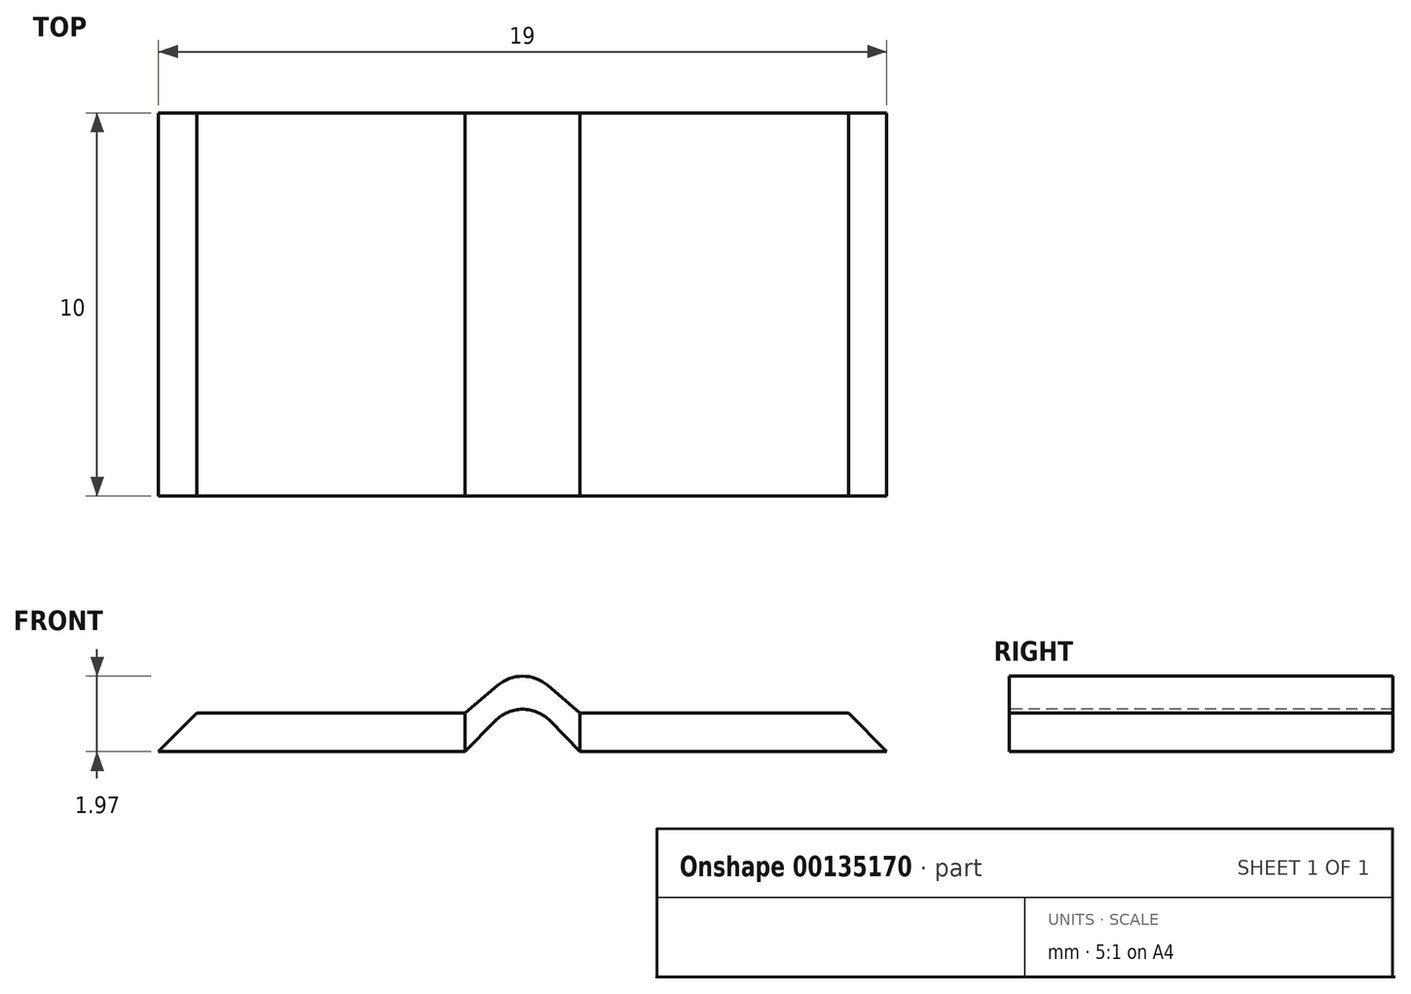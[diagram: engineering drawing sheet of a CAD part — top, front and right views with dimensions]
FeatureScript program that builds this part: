
annotation { "Feature Type Name" : "Feature", "Feature Type Description" : "" }
export const myFeature = defineFeature(function(context is Context, id is Id, definition is map)
    precondition{}
    {
        {
            var Q0;
            Q0=qCreatedBy(makeId("Top.planeOp"),FACE);
            var sketch = newSketch(context, id + "F0", { "sketchPlane" : qUnion([Q0])});
            skLineSegment(sketch, "E0.bottom", {"start": v(-2.99, 1.84) * mm, "end": v(5.01, 1.84) * mm});
            skLineSegment(sketch, "E0.top", {"start": v(-2.99, -8.16) * mm, "end": v(5.01, -8.16) * mm});
            skLineSegment(sketch, "E0.left", {"start": v(-2.99, 1.84) * mm, "end": v(-2.99, -8.16) * mm});
            skLineSegment(sketch, "E0.right", {"start": v(5.01, 1.84) * mm, "end": v(5.01, -8.16) * mm});
            skLineSegment(sketch, "E1", {"start": v(5.01, 1.84) * mm, "end": v(8.01, 1.84) * mm});
            skLineSegment(sketch, "E2.bottom", {"start": v(8.01, 1.84) * mm, "end": v(16.01, 1.84) * mm});
            skLineSegment(sketch, "E2.top", {"start": v(8.01, -8.16) * mm, "end": v(16.01, -8.16) * mm});
            skLineSegment(sketch, "E2.left", {"start": v(8.01, 1.84) * mm, "end": v(8.01, -8.16) * mm});
            skLineSegment(sketch, "E2.right", {"start": v(16.01, 1.84) * mm, "end": v(16.01, -8.16) * mm});
            skSolve(sketch);
        }
        {
            var Q0;
            Q0 = qSketchRegion(id + "F0", true);
            extrude(context, id + "F1", {"entities" : qUnion([Q0]), "depth" : 1 * mm});
        }
        {
            var Q0;
            Q0=makeQuery(id+"F1.opExtrude","SWEPT_FACE",FACE,{"disambiguationData":[OSD([sQuery(id+"F0.wireOp",EDGE,"E2.bottom")])]});
            var sketch = newSketch(context, id + "F2", { "sketchPlane" : qUnion([Q0])});
            skPoint(sketch, "E3.0", {"position": v(-5.01, 1) * mm});
            skPoint(sketch, "E4.0", {"position": v(-5.01, 0) * mm});
            skPoint(sketch, "E5", {"position": v(-6.51, 2.28) * mm});
            skLineSegment(sketch, "E6", {"start": v(-8.01, 1) * mm, "end": v(-6.51, 2.28) * mm});
            skLineSegment(sketch, "E7", {"start": v(-5.01, 1) * mm, "end": v(-6.51, 2.28) * mm});
            skLineSegment(sketch, "E8", {"start": v(-8.01, 1) * mm, "end": v(-8.01, 0) * mm});
            skLineSegment(sketch, "E9", {"start": v(-5.01, 0) * mm, "end": v(-5.01, 1) * mm});
            skLineSegment(sketch, "E10", {"start": v(-8.01, 0) * mm, "end": v(-6.51, 1.53) * mm});
            skLineSegment(sketch, "E11", {"start": v(-6.51, 1.53) * mm, "end": v(-5.01, 0) * mm});
            skSolve(sketch);
        }
        {
            var Q0;
            Q0 = qSketchRegion(id + "F2", true);
            var Q1;
            Q1=makeQuery(id+"F1.opExtrude","SWEPT_FACE",FACE,{"disambiguationData":[OSD([sQuery(id+"F0.wireOp",EDGE,"E0.top")])]});
            extrude(context, id + "F3", {"entities" : qUnion([Q0]), "endBound" : BoundingType.UP_TO_SURFACE, "oppositeDirection" : true, "endBoundEntityFace" : qUnion([Q1]), "depth" : 25 * mm});
        }
        {
            var Q0;
            Q0=makeQuery(id+"F3.opExtrude","SWEPT_EDGE",EDGE,{"disambiguationData":[OSD([sQuery(id+"F2.wireOp",EDGE,"E10"),sQuery(id+"F2.wireOp",EDGE,"E11")])]});
            var Q1;
            Q1=makeQuery(id+"F3.opExtrude","SWEPT_EDGE",EDGE,{"disambiguationData":[OSD([sQuery(id+"F2.wireOp",EDGE,"E6"),sQuery(id+"F2.wireOp",EDGE,"E7")])]});
            fillet(context, id + "F4", {"entities" : qUnion([Q0, Q1]), "radius" : 1 * mm, "tangentPropagation" : true, "allowEdgeOverflow" : false});
        }
        {
            var Q0;
            Q0=makeQuery(id+"F1.opExtrude","CAP_EDGE",EDGE,{"disambiguationData":[OSD([sQuery(id+"F0.wireOp",EDGE,"E0.left")])],"isStart":false});
            var Q1;
            Q1=makeQuery(id+"F1.opExtrude","CAP_EDGE",EDGE,{"disambiguationData":[OSD([sQuery(id+"F0.wireOp",EDGE,"E2.right")])],"isStart":false});
            chamfer(context, id + "F5", {"entities" : qUnion([Q0, Q1]), "width" : 1 * mm, "tangentPropagation" : true});
        }
    });
